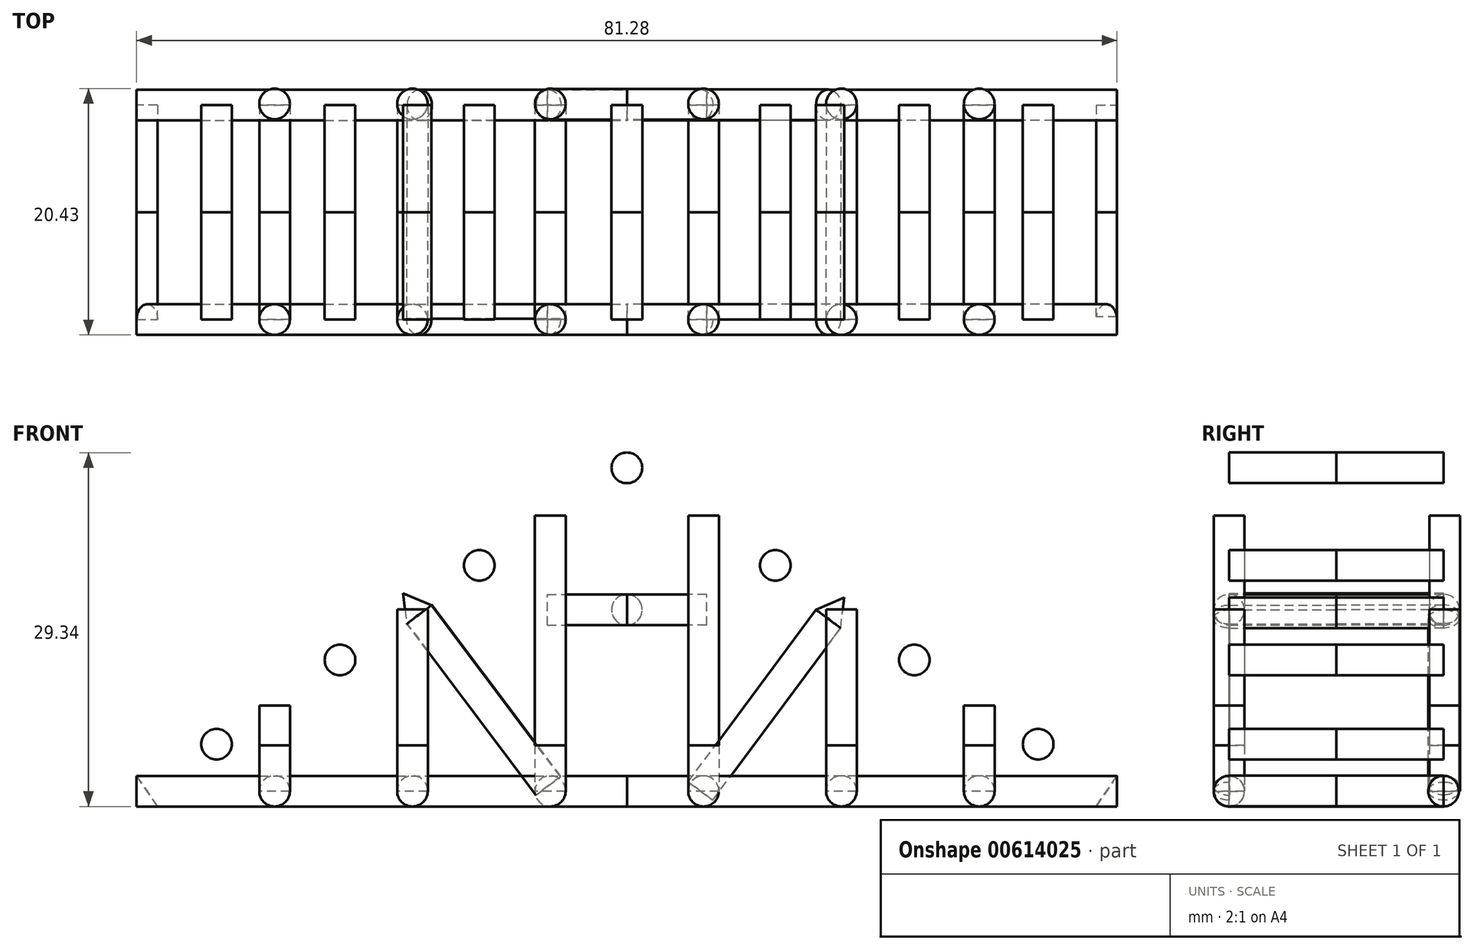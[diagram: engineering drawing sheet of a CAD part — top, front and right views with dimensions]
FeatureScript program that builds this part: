
annotation { "Feature Type Name" : "Feature", "Feature Type Description" : "" }
export const myFeature = defineFeature(function(context is Context, id is Id, definition is map)
    precondition{}
    {
        {
            var Q0;
            Q0=qCreatedBy(makeId("Right.planeOp"),FACE);
            var sketch = newSketch(context, id + "F0", { "sketchPlane" : qUnion([Q0])});
            skCircle(sketch, "E0", {"center": v(-8.9, 0) * mm, "radius": 1.27 * mm});
            skCircle(sketch, "E1", {"center": v(8.9, 0) * mm, "radius": 1.27 * mm});
            skSolve(sketch);
        }
        {
            var Q0;
            Q0=makeQuery(id+"F0.imprint","IMPRINT",FACE,{"disambiguationData":[TD([[makeQuery(id+"F0.imprint","IMPRINT",EDGE,{"derivedFrom":sQuery(id+"F0.wireOp",EDGE,"E0")}),1.0]])]});
            var Q1;
            Q1=makeQuery(id+"F0.imprint","IMPRINT",FACE,{"disambiguationData":[TD([[makeQuery(id+"F0.imprint","IMPRINT",EDGE,{"derivedFrom":sQuery(id+"F0.wireOp",EDGE,"E1")}),1.0]])]});
            extrude(context, id + "F1", {"entities" : qUnion([Q0, Q1]), "depth" : 40.64 * mm, "offsetDistance" : 25.4 * mm});
        }
        {
            var Q0;
            Q0=makeQuery(id+"F0.imprint","IMPRINT",FACE,{"disambiguationData":[TD([[makeQuery(id+"F0.imprint","IMPRINT",EDGE,{"derivedFrom":sQuery(id+"F0.wireOp",EDGE,"E0")}),1.0]])]});
            var Q1;
            Q1=makeQuery(id+"F0.imprint","IMPRINT",FACE,{"disambiguationData":[TD([[makeQuery(id+"F0.imprint","IMPRINT",EDGE,{"derivedFrom":sQuery(id+"F0.wireOp",EDGE,"E1")}),1.0]])]});
            extrude(context, id + "F2", {"entities" : qUnion([Q0, Q1]), "oppositeDirection" : true, "depth" : 40.64 * mm, "offsetDistance" : 25.4 * mm});
        }
        {
            var Q0;
            Q0=qCreatedBy(makeId("Top.planeOp"),FACE);
            var sketch = newSketch(context, id + "F3", { "sketchPlane" : qUnion([Q0])});
            skCircle(sketch, "E2", {"center": v(-29.21, -8.9) * mm, "radius": 1.27 * mm});
            skCircle(sketch, "E3", {"center": v(-17.78, -8.9) * mm, "radius": 1.27 * mm});
            skCircle(sketch, "E4", {"center": v(-6.35, -8.9) * mm, "radius": 1.27 * mm});
            skCircle(sketch, "E5", {"center": v(6.35, -8.9) * mm, "radius": 1.27 * mm});
            skCircle(sketch, "E6", {"center": v(17.78, -8.9) * mm, "radius": 1.27 * mm});
            skCircle(sketch, "E7", {"center": v(29.21, -8.9) * mm, "radius": 1.27 * mm});
            skCircle(sketch, "E8", {"center": v(-29.21, 9) * mm, "radius": 1.27 * mm});
            skCircle(sketch, "E9", {"center": v(-17.78, 9) * mm, "radius": 1.27 * mm});
            skCircle(sketch, "E10", {"center": v(-6.35, 9) * mm, "radius": 1.27 * mm});
            skCircle(sketch, "E11", {"center": v(6.35, 9) * mm, "radius": 1.27 * mm});
            skCircle(sketch, "E12", {"center": v(17.78, 9) * mm, "radius": 1.27 * mm});
            skCircle(sketch, "E13", {"center": v(29.21, 9) * mm, "radius": 1.27 * mm});
            skSolve(sketch);
        }
        {
            var Q0;
            Q0=makeQuery(id+"F3.imprint","IMPRINT",FACE,{"disambiguationData":[TD([[makeQuery(id+"F3.imprint","IMPRINT",EDGE,{"derivedFrom":sQuery(id+"F3.wireOp",EDGE,"E2")}),1.0]])]});
            var Q1;
            Q1=makeQuery(id+"F3.imprint","IMPRINT",FACE,{"disambiguationData":[TD([[makeQuery(id+"F3.imprint","IMPRINT",EDGE,{"derivedFrom":sQuery(id+"F3.wireOp",EDGE,"E3")}),1.0]])]});
            var Q2;
            Q2=makeQuery(id+"F3.imprint","IMPRINT",FACE,{"disambiguationData":[TD([[makeQuery(id+"F3.imprint","IMPRINT",EDGE,{"derivedFrom":sQuery(id+"F3.wireOp",EDGE,"E4")}),1.0]])]});
            var Q3;
            Q3=makeQuery(id+"F3.imprint","IMPRINT",FACE,{"disambiguationData":[TD([[makeQuery(id+"F3.imprint","IMPRINT",EDGE,{"derivedFrom":sQuery(id+"F3.wireOp",EDGE,"E5")}),1.0]])]});
            var Q4;
            Q4=makeQuery(id+"F3.imprint","IMPRINT",FACE,{"disambiguationData":[TD([[makeQuery(id+"F3.imprint","IMPRINT",EDGE,{"derivedFrom":sQuery(id+"F3.wireOp",EDGE,"E6")}),1.0]])]});
            var Q5;
            Q5=makeQuery(id+"F3.imprint","IMPRINT",FACE,{"disambiguationData":[TD([[makeQuery(id+"F3.imprint","IMPRINT",EDGE,{"derivedFrom":sQuery(id+"F3.wireOp",EDGE,"E7")}),1.0]])]});
            var Q6;
            Q6=makeQuery(id+"F3.imprint","IMPRINT",FACE,{"disambiguationData":[TD([[makeQuery(id+"F3.imprint","IMPRINT",EDGE,{"derivedFrom":sQuery(id+"F3.wireOp",EDGE,"E13")}),1.0]])]});
            var Q7;
            Q7=makeQuery(id+"F3.imprint","IMPRINT",FACE,{"disambiguationData":[TD([[makeQuery(id+"F3.imprint","IMPRINT",EDGE,{"derivedFrom":sQuery(id+"F3.wireOp",EDGE,"E12")}),1.0]])]});
            var Q8;
            Q8=makeQuery(id+"F3.imprint","IMPRINT",FACE,{"disambiguationData":[TD([[makeQuery(id+"F3.imprint","IMPRINT",EDGE,{"derivedFrom":sQuery(id+"F3.wireOp",EDGE,"E11")}),1.0]])]});
            var Q9;
            Q9=makeQuery(id+"F3.imprint","IMPRINT",FACE,{"disambiguationData":[TD([[makeQuery(id+"F3.imprint","IMPRINT",EDGE,{"derivedFrom":sQuery(id+"F3.wireOp",EDGE,"E10")}),1.0]])]});
            var Q10;
            Q10=makeQuery(id+"F3.imprint","IMPRINT",FACE,{"disambiguationData":[TD([[makeQuery(id+"F3.imprint","IMPRINT",EDGE,{"derivedFrom":sQuery(id+"F3.wireOp",EDGE,"E9")}),1.0]])]});
            var Q11;
            Q11=makeQuery(id+"F3.imprint","IMPRINT",FACE,{"disambiguationData":[TD([[makeQuery(id+"F3.imprint","IMPRINT",EDGE,{"derivedFrom":sQuery(id+"F3.wireOp",EDGE,"E8")}),1.0]])]});
            extrude(context, id + "F4", {"entities" : qUnion([Q0, Q1, Q2, Q3, Q4, Q5, Q6, Q7, Q8, Q9, Q10, Q11]), "depth" : 3.8 * mm, "offsetDistance" : 25.4 * mm});
        }
        {
            var Q0;
            Q0=qCreatedBy(makeId("Front.planeOp"),FACE);
            var sketch = newSketch(context, id + "F5", { "sketchPlane" : qUnion([Q0])});
            skLineSegment(sketch, "E14", {"start": v(-40.64, 1.27) * mm, "end": v(-40.64, -1.27) * mm});
            skLineSegment(sketch, "E15", {"start": v(-40.64, -1.27) * mm, "end": v(-38.91, -1.27) * mm});
            skLineSegment(sketch, "E16", {"start": v(-38.91, -1.27) * mm, "end": v(-40.64, 1.27) * mm});
            skLineSegment(sketch, "E17", {"start": v(40.64, 1.29) * mm, "end": v(40.64, -1.25) * mm});
            skLineSegment(sketch, "E18", {"start": v(40.64, -1.25) * mm, "end": v(38.91, -1.25) * mm});
            skLineSegment(sketch, "E19", {"start": v(38.91, -1.25) * mm, "end": v(40.64, 1.29) * mm});
            skCircle(sketch, "E20", {"center": v(-29.21, 0) * mm, "radius": 1.27 * mm});
            skCircle(sketch, "E21", {"center": v(-17.78, 0) * mm, "radius": 1.27 * mm});
            skCircle(sketch, "E22", {"center": v(-6.35, 0) * mm, "radius": 1.27 * mm});
            skCircle(sketch, "E23", {"center": v(6.35, 0) * mm, "radius": 1.27 * mm});
            skCircle(sketch, "E24", {"center": v(17.78, 0) * mm, "radius": 1.27 * mm});
            skCircle(sketch, "E25", {"center": v(29.21, 0) * mm, "radius": 1.27 * mm});
            skSolve(sketch);
        }
        {
            var Q0;
            Q0=makeQuery(id+"F5.imprint","IMPRINT",FACE,{"disambiguationData":[TD([[makeQuery(id+"F5.imprint","IMPRINT",EDGE,{"derivedFrom":sQuery(id+"F5.wireOp",EDGE,"E14")}),1.0]])]});
            extrude(context, id + "F6", {"entities" : qUnion([Q0]), "operationType" : NewBodyOperationType.ADD, "depth" : 8.9 * mm, "offsetDistance" : 25.4 * mm});
        }
        {
            var Q0;
            Q0=makeQuery(id+"F5.imprint","IMPRINT",FACE,{"disambiguationData":[TD([[makeQuery(id+"F5.imprint","IMPRINT",EDGE,{"derivedFrom":sQuery(id+"F5.wireOp",EDGE,"E14")}),1.0]])]});
            extrude(context, id + "F7", {"entities" : qUnion([Q0]), "oppositeDirection" : true, "depth" : 8.9 * mm, "offsetDistance" : 25.4 * mm});
        }
        {
            var Q0;
            Q0=makeQuery(id+"F6.opExtrude","SWEPT_FACE",FACE,{"disambiguationData":[OSD([sQuery(id+"F5.wireOp",EDGE,"E16")])]});
            var sketch = newSketch(context, id + "F8", { "sketchPlane" : qUnion([Q0])});
            skCircle(sketch, "E26", {"center": v(-8.9, 22.37) * mm, "radius": 1.27 * mm});
            skCircle(sketch, "E27", {"center": v(8.94, 22.48) * mm, "radius": 1.27 * mm});
            skSolve(sketch);
        }
        {
            var Q0;
            Q0=sQuery(id+"F8.wireOp",EDGE,"E27");
            extrude(context, id + "F9", {"bodyType" : ToolBodyType.SURFACE, "surfaceEntities" : qUnion([Q0]), "depth" : 49.07 * mm, "offsetDistance" : 25.4 * mm});
        }
        {
            var Q0;
            Q0=sQuery(id+"F8.wireOp",EDGE,"E26");
            extrude(context, id + "F10", {"bodyType" : ToolBodyType.SURFACE, "surfaceEntities" : qUnion([Q0]), "depth" : 49.07 * mm, "offsetDistance" : 25.4 * mm});
        }
        {
            var Q0;
            Q0=makeQuery(id+"F5.imprint","IMPRINT",FACE,{"disambiguationData":[TD([[makeQuery(id+"F5.imprint","IMPRINT",EDGE,{"derivedFrom":sQuery(id+"F5.wireOp",EDGE,"E17")}),-1.0]])]});
            extrude(context, id + "F11", {"entities" : qUnion([Q0]), "operationType" : NewBodyOperationType.ADD, "depth" : 8.9 * mm, "offsetDistance" : 25.4 * mm});
        }
        {
            var Q0;
            Q0=makeQuery(id+"F5.imprint","IMPRINT",FACE,{"disambiguationData":[TD([[makeQuery(id+"F5.imprint","IMPRINT",EDGE,{"derivedFrom":sQuery(id+"F5.wireOp",EDGE,"E17")}),-1.0]])]});
            extrude(context, id + "F12", {"entities" : qUnion([Q0]), "oppositeDirection" : true, "depth" : 8.9 * mm, "offsetDistance" : 25.4 * mm});
        }
        {
            var Q0;
            Q0=makeQuery(id+"F12.opExtrude","SWEPT_FACE",FACE,{"disambiguationData":[OSD([sQuery(id+"F5.wireOp",EDGE,"E19")])]});
            var sketch = newSketch(context, id + "F13", { "sketchPlane" : qUnion([Q0])});
            skCircle(sketch, "E28", {"center": v(-8.9, 22.38) * mm, "radius": 1.27 * mm});
            skCircle(sketch, "E29", {"center": v(8.9, 22.38) * mm, "radius": 1.27 * mm});
            skSolve(sketch);
        }
        {
            var Q0;
            Q0=sQuery(id+"F13.wireOp",EDGE,"E29");
            extrude(context, id + "F14", {"bodyType" : ToolBodyType.SURFACE, "surfaceEntities" : qUnion([Q0]), "depth" : 48.94 * mm, "offsetDistance" : 25.4 * mm});
        }
        {
            var Q0;
            Q0=sQuery(id+"F13.wireOp",EDGE,"E28");
            extrude(context, id + "F15", {"bodyType" : ToolBodyType.SURFACE, "surfaceEntities" : qUnion([Q0]), "depth" : 49.07 * mm, "offsetDistance" : 25.4 * mm});
        }
        {
            var Q0;
            Q0=makeQuery(id+"F4.opExtrude","CAP_FACE",FACE,{"disambiguationData":[OSD([sQuery(id+"F3.wireOp",EDGE,"E2")])],"isStart":false});
            var Q1;
            Q1=makeQuery(id+"F4.opExtrude","CAP_FACE",FACE,{"disambiguationData":[OSD([sQuery(id+"F3.wireOp",EDGE,"E7")])],"isStart":false});
            var Q2;
            Q2=makeQuery(id+"F4.opExtrude","CAP_FACE",FACE,{"disambiguationData":[OSD([sQuery(id+"F3.wireOp",EDGE,"E8")])],"isStart":false});
            var Q3;
            Q3=makeQuery(id+"F4.opExtrude","CAP_FACE",FACE,{"disambiguationData":[OSD([sQuery(id+"F3.wireOp",EDGE,"E13")])],"isStart":false});
            extrude(context, id + "F16", {"entities" : qUnion([Q0, Q1, Q2, Q3]), "depth" : 3.3 * mm, "offsetDistance" : 25.4 * mm});
        }
        {
            var Q0;
            Q0=makeQuery(id+"F4.opExtrude","CAP_FACE",FACE,{"disambiguationData":[OSD([sQuery(id+"F3.wireOp",EDGE,"E9")])],"isStart":false});
            var Q1;
            Q1=makeQuery(id+"F4.opExtrude","CAP_FACE",FACE,{"disambiguationData":[OSD([sQuery(id+"F3.wireOp",EDGE,"E3")])],"isStart":false});
            var Q2;
            Q2=makeQuery(id+"F4.opExtrude","CAP_FACE",FACE,{"disambiguationData":[OSD([sQuery(id+"F3.wireOp",EDGE,"E12")])],"isStart":false});
            var Q3;
            Q3=makeQuery(id+"F4.opExtrude","CAP_FACE",FACE,{"disambiguationData":[OSD([sQuery(id+"F3.wireOp",EDGE,"E6")])],"isStart":false});
            extrude(context, id + "F17", {"entities" : qUnion([Q0, Q1, Q2, Q3]), "depth" : 11.25 * mm, "offsetDistance" : 25.4 * mm});
        }
        {
            var Q0;
            Q0=makeQuery(id+"F4.opExtrude","CAP_FACE",FACE,{"disambiguationData":[OSD([sQuery(id+"F3.wireOp",EDGE,"E4")])],"isStart":false});
            var Q1;
            Q1=makeQuery(id+"F4.opExtrude","CAP_FACE",FACE,{"disambiguationData":[OSD([sQuery(id+"F3.wireOp",EDGE,"E10")])],"isStart":false});
            var Q2;
            Q2=makeQuery(id+"F4.opExtrude","CAP_FACE",FACE,{"disambiguationData":[OSD([sQuery(id+"F3.wireOp",EDGE,"E11")])],"isStart":false});
            var Q3;
            Q3=makeQuery(id+"F4.opExtrude","CAP_FACE",FACE,{"disambiguationData":[OSD([sQuery(id+"F3.wireOp",EDGE,"E5")])],"isStart":false});
            extrude(context, id + "F18", {"entities" : qUnion([Q0, Q1, Q2, Q3]), "depth" : 19.02 * mm, "offsetDistance" : 25.4 * mm});
        }
        {
            var Q0;
            Q0=makeQuery(id+"F5.imprint","IMPRINT",FACE,{"disambiguationData":[TD([[makeQuery(id+"F5.imprint","IMPRINT",EDGE,{"derivedFrom":sQuery(id+"F5.wireOp",EDGE,"E20")}),1.0]])]});
            var Q1;
            Q1=makeQuery(id+"F5.imprint","IMPRINT",FACE,{"disambiguationData":[TD([[makeQuery(id+"F5.imprint","IMPRINT",EDGE,{"derivedFrom":sQuery(id+"F5.wireOp",EDGE,"E21")}),1.0]])]});
            var Q2;
            Q2=makeQuery(id+"F5.imprint","IMPRINT",FACE,{"disambiguationData":[TD([[makeQuery(id+"F5.imprint","IMPRINT",EDGE,{"derivedFrom":sQuery(id+"F5.wireOp",EDGE,"E22")}),1.0]])]});
            var Q3;
            Q3=makeQuery(id+"F5.imprint","IMPRINT",FACE,{"disambiguationData":[TD([[makeQuery(id+"F5.imprint","IMPRINT",EDGE,{"derivedFrom":sQuery(id+"F5.wireOp",EDGE,"E23")}),1.0]])]});
            var Q4;
            Q4=makeQuery(id+"F5.imprint","IMPRINT",FACE,{"disambiguationData":[TD([[makeQuery(id+"F5.imprint","IMPRINT",EDGE,{"derivedFrom":sQuery(id+"F5.wireOp",EDGE,"E24")}),1.0]])]});
            var Q5;
            Q5=makeQuery(id+"F5.imprint","IMPRINT",FACE,{"disambiguationData":[TD([[makeQuery(id+"F5.imprint","IMPRINT",EDGE,{"derivedFrom":sQuery(id+"F5.wireOp",EDGE,"E25")}),1.0]])]});
            extrude(context, id + "F19", {"entities" : qUnion([Q0, Q1, Q2, Q3, Q4, Q5]), "depth" : 8.9 * mm, "offsetDistance" : 25.4 * mm});
        }
        {
            var Q0;
            Q0=makeQuery(id+"F19.opExtrude","CAP_FACE",FACE,{"disambiguationData":[OSD([sQuery(id+"F5.wireOp",EDGE,"E20")])],"isStart":true});
            var Q1;
            Q1=makeQuery(id+"F19.opExtrude","CAP_FACE",FACE,{"disambiguationData":[OSD([sQuery(id+"F5.wireOp",EDGE,"E21")])],"isStart":true});
            var Q2;
            Q2=makeQuery(id+"F19.opExtrude","CAP_FACE",FACE,{"disambiguationData":[OSD([sQuery(id+"F5.wireOp",EDGE,"E22")])],"isStart":true});
            var Q3;
            Q3=makeQuery(id+"F19.opExtrude","CAP_FACE",FACE,{"disambiguationData":[OSD([sQuery(id+"F5.wireOp",EDGE,"E23")])],"isStart":true});
            var Q4;
            Q4=makeQuery(id+"F19.opExtrude","CAP_FACE",FACE,{"disambiguationData":[OSD([sQuery(id+"F5.wireOp",EDGE,"E24")])],"isStart":true});
            var Q5;
            Q5=makeQuery(id+"F19.opExtrude","CAP_FACE",FACE,{"disambiguationData":[OSD([sQuery(id+"F5.wireOp",EDGE,"E25")])],"isStart":true});
            extrude(context, id + "F20", {"entities" : qUnion([Q0, Q1, Q2, Q3, Q4, Q5]), "depth" : 8.9 * mm, "offsetDistance" : 25.4 * mm});
        }
        {
            var Q0;
            Q0=qCreatedBy(makeId("Front.planeOp"),FACE);
            var sketch = newSketch(context, id + "F21", { "sketchPlane" : qUnion([Q0])});
            skCircle(sketch, "E30", {"center": v(12.3, 18.72) * mm, "radius": 1.27 * mm});
            skCircle(sketch, "E31", {"center": v(23.83, 10.87) * mm, "radius": 1.27 * mm});
            skCircle(sketch, "E32", {"center": v(34.1, 3.9) * mm, "radius": 1.27 * mm});
            skCircle(sketch, "E33", {"center": v(0, 26.8) * mm, "radius": 1.27 * mm});
            skCircle(sketch, "E34", {"center": v(-12.24, 18.72) * mm, "radius": 1.27 * mm});
            skCircle(sketch, "E35", {"center": v(-23.79, 10.87) * mm, "radius": 1.27 * mm});
            skCircle(sketch, "E36", {"center": v(-34.02, 3.9) * mm, "radius": 1.27 * mm});
            skLineSegment(sketch, "E37", {"start": v(15.68, 15.04) * mm, "end": v(17.72, 13.52) * mm});
            skLineSegment(sketch, "E38", {"start": v(17.72, 13.52) * mm, "end": v(18.01, 16.05) * mm});
            skLineSegment(sketch, "E39", {"start": v(18.01, 16.05) * mm, "end": v(15.68, 15.04) * mm});
            skLineSegment(sketch, "E40", {"start": v(-18.55, 16.4) * mm, "end": v(-18.24, 13.88) * mm});
            skLineSegment(sketch, "E41", {"start": v(-18.24, 13.88) * mm, "end": v(-16.21, 15.4) * mm});
            skLineSegment(sketch, "E42", {"start": v(-16.21, 15.4) * mm, "end": v(-18.55, 16.4) * mm});
            skSolve(sketch);
        }
        {
            var Q0;
            Q0=makeQuery(id+"F21.imprint","IMPRINT",FACE,{"disambiguationData":[TD([[makeQuery(id+"F21.imprint","IMPRINT",EDGE,{"derivedFrom":sQuery(id+"F21.wireOp",EDGE,"E30")}),1.0]])]});
            var Q1;
            Q1=makeQuery(id+"F21.imprint","IMPRINT",FACE,{"disambiguationData":[TD([[makeQuery(id+"F21.imprint","IMPRINT",EDGE,{"derivedFrom":sQuery(id+"F21.wireOp",EDGE,"E33")}),1.0]])]});
            var Q2;
            Q2=makeQuery(id+"F21.imprint","IMPRINT",FACE,{"disambiguationData":[TD([[makeQuery(id+"F21.imprint","IMPRINT",EDGE,{"derivedFrom":sQuery(id+"F21.wireOp",EDGE,"E34")}),1.0]])]});
            var Q3;
            Q3=makeQuery(id+"F21.imprint","IMPRINT",FACE,{"disambiguationData":[TD([[makeQuery(id+"F21.imprint","IMPRINT",EDGE,{"derivedFrom":sQuery(id+"F21.wireOp",EDGE,"E35")}),1.0]])]});
            var Q4;
            Q4=makeQuery(id+"F21.imprint","IMPRINT",FACE,{"disambiguationData":[TD([[makeQuery(id+"F21.imprint","IMPRINT",EDGE,{"derivedFrom":sQuery(id+"F21.wireOp",EDGE,"E31")}),1.0]])]});
            var Q5;
            Q5=makeQuery(id+"F21.imprint","IMPRINT",FACE,{"disambiguationData":[TD([[makeQuery(id+"F21.imprint","IMPRINT",EDGE,{"derivedFrom":sQuery(id+"F21.wireOp",EDGE,"E32")}),1.0]])]});
            var Q6;
            Q6=makeQuery(id+"F21.imprint","IMPRINT",FACE,{"disambiguationData":[TD([[makeQuery(id+"F21.imprint","IMPRINT",EDGE,{"derivedFrom":sQuery(id+"F21.wireOp",EDGE,"E36")}),1.0]])]});
            extrude(context, id + "F22", {"entities" : qUnion([Q0, Q1, Q2, Q3, Q4, Q5, Q6]), "depth" : 8.9 * mm, "offsetDistance" : 25.4 * mm});
        }
        {
            var Q0;
            Q0=makeQuery(id+"F21.imprint","IMPRINT",FACE,{"disambiguationData":[TD([[makeQuery(id+"F21.imprint","IMPRINT",EDGE,{"derivedFrom":sQuery(id+"F21.wireOp",EDGE,"E33")}),1.0]])]});
            var Q1;
            Q1=makeQuery(id+"F21.imprint","IMPRINT",FACE,{"disambiguationData":[TD([[makeQuery(id+"F21.imprint","IMPRINT",EDGE,{"derivedFrom":sQuery(id+"F21.wireOp",EDGE,"E30")}),1.0]])]});
            var Q2;
            Q2=makeQuery(id+"F21.imprint","IMPRINT",FACE,{"disambiguationData":[TD([[makeQuery(id+"F21.imprint","IMPRINT",EDGE,{"derivedFrom":sQuery(id+"F21.wireOp",EDGE,"E34")}),1.0]])]});
            var Q3;
            Q3=makeQuery(id+"F21.imprint","IMPRINT",FACE,{"disambiguationData":[TD([[makeQuery(id+"F21.imprint","IMPRINT",EDGE,{"derivedFrom":sQuery(id+"F21.wireOp",EDGE,"E35")}),1.0]])]});
            var Q4;
            Q4=makeQuery(id+"F21.imprint","IMPRINT",FACE,{"disambiguationData":[TD([[makeQuery(id+"F21.imprint","IMPRINT",EDGE,{"derivedFrom":sQuery(id+"F21.wireOp",EDGE,"E31")}),1.0]])]});
            var Q5;
            Q5=makeQuery(id+"F21.imprint","IMPRINT",FACE,{"disambiguationData":[TD([[makeQuery(id+"F21.imprint","IMPRINT",EDGE,{"derivedFrom":sQuery(id+"F21.wireOp",EDGE,"E36")}),1.0]])]});
            var Q6;
            Q6=makeQuery(id+"F21.imprint","IMPRINT",FACE,{"disambiguationData":[TD([[makeQuery(id+"F21.imprint","IMPRINT",EDGE,{"derivedFrom":sQuery(id+"F21.wireOp",EDGE,"E32")}),1.0]])]});
            extrude(context, id + "F23", {"entities" : qUnion([Q0, Q1, Q2, Q3, Q4, Q5, Q6]), "oppositeDirection" : true, "depth" : 8.9 * mm, "offsetDistance" : 25.4 * mm});
        }
        {
            var Q0;
            Q0=qCreatedBy(makeId("Right.planeOp"),FACE);
            var sketch = newSketch(context, id + "F24", { "sketchPlane" : qUnion([Q0])});
            skCircle(sketch, "E43", {"center": v(8.94, 15.03) * mm, "radius": 1.27 * mm});
            skCircle(sketch, "E44", {"center": v(-8.9, 15.03) * mm, "radius": 1.27 * mm});
            skSolve(sketch);
        }
        {
            var Q0;
            Q0=makeQuery(id+"F24.imprint","IMPRINT",FACE,{"disambiguationData":[TD([[makeQuery(id+"F24.imprint","IMPRINT",EDGE,{"derivedFrom":sQuery(id+"F24.wireOp",EDGE,"E43")}),1.0]])]});
            var Q1;
            Q1=makeQuery(id+"F24.imprint","IMPRINT",FACE,{"disambiguationData":[TD([[makeQuery(id+"F24.imprint","IMPRINT",EDGE,{"derivedFrom":sQuery(id+"F24.wireOp",EDGE,"E44")}),1.0]])]});
            extrude(context, id + "F25", {"entities" : qUnion([Q0, Q1]), "depth" : 6.6 * mm, "offsetDistance" : 25.4 * mm});
        }
        {
            var Q0;
            Q0=makeQuery(id+"F24.imprint","IMPRINT",FACE,{"disambiguationData":[TD([[makeQuery(id+"F24.imprint","IMPRINT",EDGE,{"derivedFrom":sQuery(id+"F24.wireOp",EDGE,"E44")}),1.0]])]});
            var Q1;
            Q1=makeQuery(id+"F24.imprint","IMPRINT",FACE,{"disambiguationData":[TD([[makeQuery(id+"F24.imprint","IMPRINT",EDGE,{"derivedFrom":sQuery(id+"F24.wireOp",EDGE,"E43")}),1.0]])]});
            extrude(context, id + "F26", {"entities" : qUnion([Q0, Q1]), "oppositeDirection" : true, "depth" : 6.6 * mm, "offsetDistance" : 25.4 * mm});
        }
        {
            var Q0;
            Q0=makeQuery(id+"F21.imprint","IMPRINT",FACE,{"disambiguationData":[TD([[makeQuery(id+"F21.imprint","IMPRINT",EDGE,{"derivedFrom":sQuery(id+"F21.wireOp",EDGE,"E37")}),1.0]])]});
            var Q1;
            Q1=makeQuery(id+"F21.imprint","IMPRINT",FACE,{"disambiguationData":[TD([[makeQuery(id+"F21.imprint","IMPRINT",EDGE,{"derivedFrom":sQuery(id+"F21.wireOp",EDGE,"E40")}),1.0]])]});
            extrude(context, id + "F27", {"entities" : qUnion([Q0, Q1]), "depth" : 8.9 * mm, "offsetDistance" : 25.4 * mm});
        }
        {
            var Q0;
            Q0=makeQuery(id+"F21.imprint","IMPRINT",FACE,{"disambiguationData":[TD([[makeQuery(id+"F21.imprint","IMPRINT",EDGE,{"derivedFrom":sQuery(id+"F21.wireOp",EDGE,"E37")}),1.0]])]});
            var Q1;
            Q1=makeQuery(id+"F21.imprint","IMPRINT",FACE,{"disambiguationData":[TD([[makeQuery(id+"F21.imprint","IMPRINT",EDGE,{"derivedFrom":sQuery(id+"F21.wireOp",EDGE,"E40")}),1.0]])]});
            extrude(context, id + "F28", {"entities" : qUnion([Q0, Q1]), "oppositeDirection" : true, "depth" : 8.9 * mm, "offsetDistance" : 25.4 * mm});
        }
        {
            var Q0;
            Q0=makeQuery(id+"F27.opExtrude","SWEPT_FACE",FACE,{"disambiguationData":[OSD([sQuery(id+"F21.wireOp",EDGE,"E41")])]});
            var sketch = newSketch(context, id + "F29", { "sketchPlane" : qUnion([Q0])});
            skCircle(sketch, "E45", {"center": v(-4.95, 8.9) * mm, "radius": 1.27 * mm});
            skCircle(sketch, "E46", {"center": v(-4.9, -8.89) * mm, "radius": 1.27 * mm});
            skSolve(sketch);
        }
        {
            var Q0;
            Q0=makeQuery(id+"F29.imprint","IMPRINT",FACE,{"disambiguationData":[TD([[makeQuery(id+"F29.imprint","IMPRINT",EDGE,{"derivedFrom":sQuery(id+"F29.wireOp",EDGE,"E46")}),1.0]])]});
            var Q1;
            {var subQ1=sQuery(id+"F21.wireOp",EDGE,"E41");var subQ6=makeQuery(id+"F27.opExtrude","CAP_EDGE",EDGE,{"disambiguationData":[OSD([subQ1])],"isStart":false});Q1=makeQuery(id+"F29.imprint","IMPRINT",FACE,{"disambiguationData":[TD([[makeQuery(id+"F29.imprint","IMPRINT",EDGE,{"derivedFrom":subQ6}),1.0]])]});}
            extrude(context, id + "F30", {"entities" : qUnion([Q0, Q1]), "depth" : 17.78 * mm, "offsetDistance" : 25.4 * mm});
        }
        {
            var Q0;
            Q0=makeQuery(id+"F27.opExtrude","SWEPT_FACE",FACE,{"disambiguationData":[OSD([sQuery(id+"F21.wireOp",EDGE,"E37")])]});
            var sketch = newSketch(context, id + "F31", { "sketchPlane" : qUnion([Q0])});
            skCircle(sketch, "E47", {"center": v(4.89, 8.9) * mm, "radius": 1.27 * mm});
            skCircle(sketch, "E48", {"center": v(4.89, -8.91) * mm, "radius": 1.27 * mm});
            skSolve(sketch);
        }
        {
            var Q0;
            {var subQ1=sQuery(id+"F21.wireOp",EDGE,"E37");var subQ2=makeQuery(id+"F27.opExtrude","CAP_EDGE",EDGE,{"disambiguationData":[OSD([subQ1])],"isStart":false});Q0=makeQuery(id+"F31.imprint","IMPRINT",FACE,{"disambiguationData":[TD([[makeQuery(id+"F31.imprint","IMPRINT",EDGE,{"derivedFrom":subQ2}),1.0]])]});}
            var Q1;
            Q1=makeQuery(id+"F31.imprint","IMPRINT",FACE,{"disambiguationData":[TD([[makeQuery(id+"F31.imprint","IMPRINT",EDGE,{"derivedFrom":sQuery(id+"F31.wireOp",EDGE,"E48")}),1.0]])]});
            extrude(context, id + "F32", {"entities" : qUnion([Q0, Q1]), "depth" : 17.78 * mm, "offsetDistance" : 25.4 * mm});
        }
        {
            var Q0;
            Q0=qCreatedBy(makeId("Front.planeOp"),FACE);
            var sketch = newSketch(context, id + "F33", { "sketchPlane" : qUnion([Q0])});
            skCircle(sketch, "E49", {"center": v(0, 15.04) * mm, "radius": 1.27 * mm});
            skSolve(sketch);
        }
        {
            var Q0;
            Q0=makeQuery(id+"F33.imprint","IMPRINT",FACE,{"disambiguationData":[TD([[makeQuery(id+"F33.imprint","IMPRINT",EDGE,{"derivedFrom":sQuery(id+"F33.wireOp",EDGE,"E49")}),1.0]])]});
            extrude(context, id + "F34", {"entities" : qUnion([Q0]), "depth" : 8.9 * mm, "offsetDistance" : 25.4 * mm});
        }
        {
            var Q0;
            Q0=makeQuery(id+"F33.imprint","IMPRINT",FACE,{"disambiguationData":[TD([[makeQuery(id+"F33.imprint","IMPRINT",EDGE,{"derivedFrom":sQuery(id+"F33.wireOp",EDGE,"E49")}),1.0]])]});
            extrude(context, id + "F35", {"entities" : qUnion([Q0]), "oppositeDirection" : true, "depth" : 8.9 * mm, "offsetDistance" : 25.4 * mm});
        }
    });
